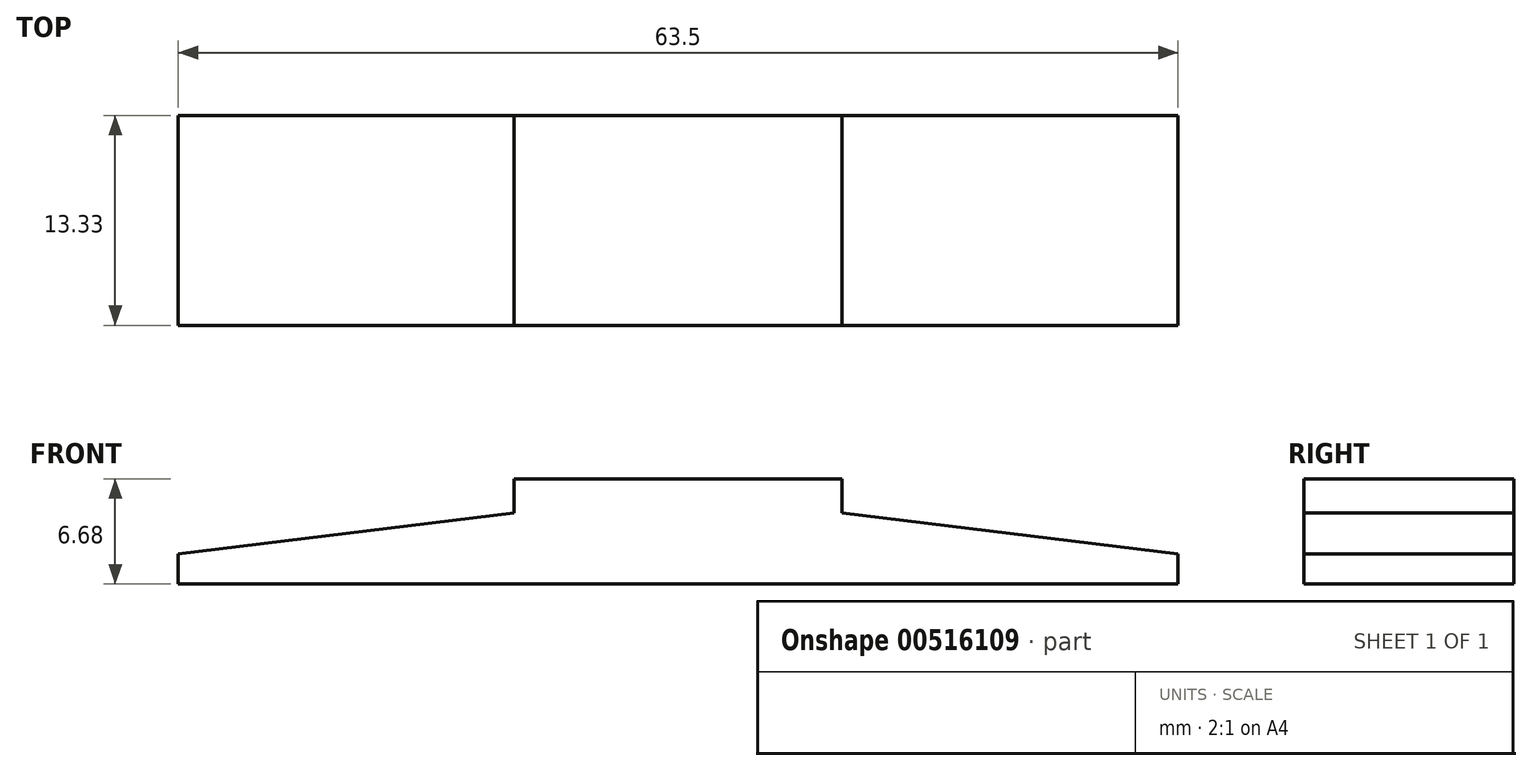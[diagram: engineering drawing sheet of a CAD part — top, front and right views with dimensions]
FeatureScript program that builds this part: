
annotation { "Feature Type Name" : "Feature", "Feature Type Description" : "" }
export const myFeature = defineFeature(function(context is Context, id is Id, definition is map)
    precondition{}
    {
        {
            var Q0;
            Q0=qCreatedBy(makeId("Front.planeOp"),FACE);
            var sketch = newSketch(context, id + "F0", { "sketchPlane" : qUnion([Q0])});
            skLineSegment(sketch, "E0", {"start": v(43.13, 34.83) * mm, "end": v(63.96, 34.83) * mm});
            skLineSegment(sketch, "E1", {"start": v(63.96, 34.83) * mm, "end": v(63.96, 32.68) * mm});
            skLineSegment(sketch, "E2", {"start": v(63.96, 32.68) * mm, "end": v(85.3, 30.06) * mm});
            skLineSegment(sketch, "E3", {"start": v(85.3, 30.06) * mm, "end": v(85.3, 28.15) * mm});
            skLineSegment(sketch, "E4", {"start": v(85.3, 28.15) * mm, "end": v(21.8, 28.15) * mm});
            skLineSegment(sketch, "E5", {"start": v(21.8, 28.15) * mm, "end": v(21.8, 30.06) * mm});
            skLineSegment(sketch, "E6", {"start": v(21.8, 30.06) * mm, "end": v(43.13, 32.68) * mm});
            skLineSegment(sketch, "E7", {"start": v(43.13, 32.68) * mm, "end": v(43.13, 34.83) * mm});
            skLineSegment(sketch, "E8", {"start": v(53.54, 34.83) * mm, "end": v(53.54, 28.15) * mm, "construction": true});
            skSolve(sketch);
        }
        {
            var Q0;
            Q0=makeQuery(id+"F0.imprint","IMPRINT",FACE,{"disambiguationData":[TD([[makeQuery(id+"F0.imprint","IMPRINT",EDGE,{"derivedFrom":sQuery(id+"F0.wireOp",EDGE,"E0")}),-1.0]])]});
            extrude(context, id + "F1", {"entities" : qUnion([Q0]), "depth" : 13.33 * mm});
        }
    });
